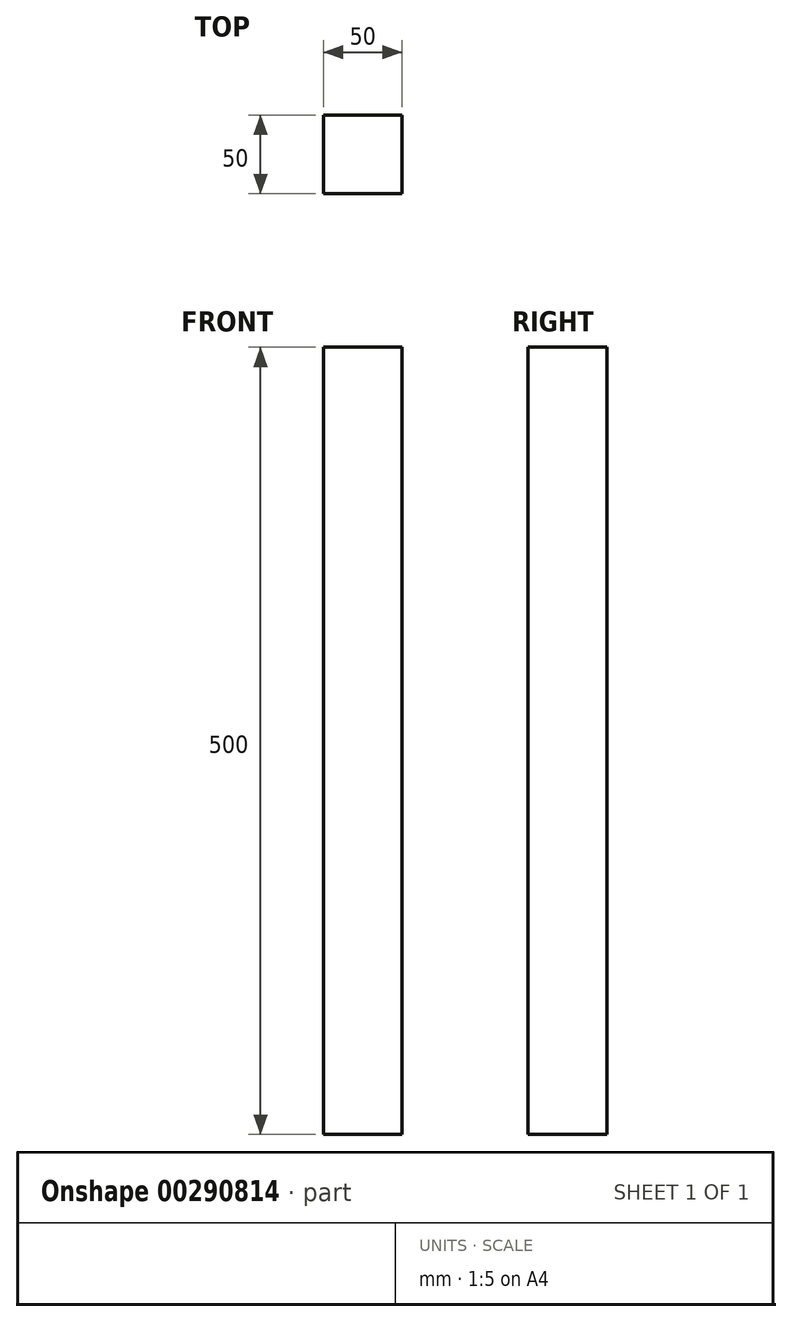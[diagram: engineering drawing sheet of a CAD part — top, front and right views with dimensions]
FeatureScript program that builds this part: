
annotation { "Feature Type Name" : "Feature", "Feature Type Description" : "" }
export const myFeature = defineFeature(function(context is Context, id is Id, definition is map)
    precondition{}
    {
        {
            var Q0;
            Q0=qCreatedBy(makeId("Top.planeOp"),FACE);
            var sketch = newSketch(context, id + "F0", { "sketchPlane" : qUnion([Q0])});
            skLineSegment(sketch, "E0.bottom", {"start": v(25, 25) * mm, "end": v(-25, 25) * mm});
            skLineSegment(sketch, "E0.top", {"start": v(25, -25) * mm, "end": v(-25, -25) * mm});
            skLineSegment(sketch, "E0.left", {"start": v(25, 25) * mm, "end": v(25, -25) * mm});
            skLineSegment(sketch, "E0.right", {"start": v(-25, 25) * mm, "end": v(-25, -25) * mm});
            skPoint(sketch, "E0.middle", {"position": v(0, 0) * mm});
            skSolve(sketch);
        }
        {
            var Q0;
            Q0 = qSketchRegion(id + "F0", true);
            extrude(context, id + "F1", {"entities" : qUnion([Q0]), "depth" : 500 * mm});
        }
    });
